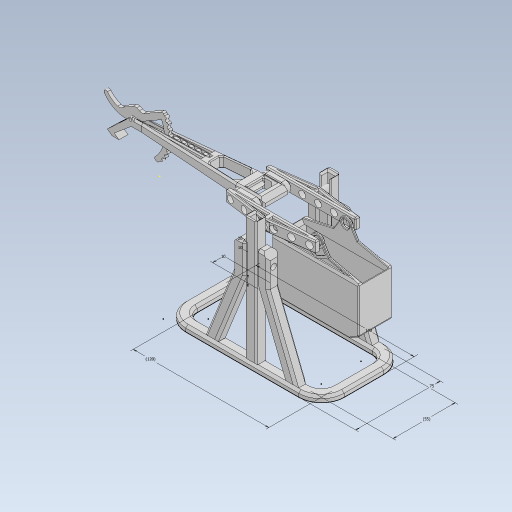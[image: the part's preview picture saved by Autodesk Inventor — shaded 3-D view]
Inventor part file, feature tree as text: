
AUTODESK INVENTOR PART (.ipt)
format: ipt  version: 2023 (Build 270158030, 158C)  size: 2,069,504 bytes
history: native  units: mm
features: extrude x39, sketch x36, chamfer x34, other x22, projected_geometry x16, mirror x11, fillet x10, plane x5, pattern_circular x2
ambient origin geometry x8: Origin, YZ Plane, XZ Plane, XY Plane, X Axis, Y Axis, Z Axis, Center Point
bodies: SOLID_WEIGHT (feature_tree)
feature tree (175):
  other  "baseplate"
  sketch  "Sketch1"  dims[d0=75.0mm d1=140.0mm]
  extrude  "Extrusion1"  Depth=140.0mm
  extrude  "Extrusion2"  Depth=10.0mm
  sketch  "Sketch3"  dims[d4=20.0mm d5=5.0mm d6=0.0mm]
  extrude  "Extrusion5"  Depth=5.0mm TaperAngle=0.0deg
  extrude  "Extrusion6"  Depth=2.0mm
  extrude  "Extrusion3"  Depth=3.0mm
  extrude  "Extrusion7"  Depth=10.0mm
  extrude  "Extrusion9"  TaperAngle=0.0deg  [1 undecoded]
  extrude  "Extrusion10"  Depth=120.0mm
  extrude  "Extrusion11"  Depth=0.01mm
  extrude  "Extrusion29"  Depth=10.0mm
  other  "center-mirror-plane"
  other  "Work Point1"
  plane  "Work Plane2"
  extrude  "Extrusion12"  Depth=25.0mm
  extrude  "Extrusion13"  Depth=5.0mm TaperAngle=0.0deg
  extrude  "Extrusion14"  Depth=10.0mm
  extrude  "Extrusion15"  Depth=10.0mm TaperAngle=0.0deg
  extrude  "Extrusion30"  Depth=5.0mm
  extrude  "Extrusion31"  Depth=6.5mm
  plane  "Work Plane5"
  extrude  "Extrusion32"  Depth=1.75mm
  extrude  "Extrusion33"  Depth=6.5mm
  extrude  "Extrusion34"  Depth=10.0mm
  fillet  "Fillet4"  Radius=3.2mm
  chamfer  "Chamfer37"  Distance=10.0mm
  extrude  "Extrusion35"  Depth=4.0mm
  chamfer  "Chamfer38"  [1 undecoded]
  fillet  "Fillet11"  Radius=21.0mm
  chamfer  "Chamfer39"  [1 undecoded]
  fillet  "Fillet12"  Radius=6.0mm
  extrude  "Extrusion36"  Depth=2.0mm
  fillet  "Fillet5"  Radius=10.0mm
  extrude  "Extrusion37"  Depth=2.0mm TaperAngle=45.0deg
  sketch  "Sketch51"  dims[d109=12.0mm d110=0.0mm d111=0.0mm d119=6.0mm d120=5.0mm d121=10.0mm d122=0.0mm d126=1.0mm d127=2.0mm d128=45.0deg d129=1.0mm d130=2.0mm d131=45.0deg d132=1.0mm d133=2.0mm d134=45.0deg d135=1.5mm d136=2.0mm d137=45.0deg d138=2.5mm d139=2.8mm d140=12.0mm d141=0.0mm d142=0.0mm d144=6.0mm d145=2.0mm d146=2.0mm d147=45.0deg d155=1.0mm d156=2.0mm d157=45.0deg d158=1.5mm d159=2.0mm d160=45.0deg d162=1.5mm d163=2.0mm d164=45.0deg d165=2.0mm d166=2.0mm d167=45.0deg d168=1.5mm d169=2.0mm d170=45.0deg d172=2.0mm d173=8.0mm d174=5.0mm d175=28.0mm d176=6.0mm d177=40.0mm d178=5.0mm d179=28.0mm d180=8.0mm d181=8.0mm d182=2.0mm d183=2.0mm d184=0.0mm d185=2.0mm d186=0.0mm d187=1.5mm d188=0.0mm d189=1.5mm d190=2.0mm d191=45.0deg d195=1.0mm d196=1.5mm d197=0.0mm d200=1.0mm d201=2.0mm d202=45.0deg d209=0.5mm d210=2.0mm d211=45.0deg d212=0.5mm d213=2.0mm d214=45.0deg d221=0.0mm d222=0.0mm d223=1.0mm d224=1.0mm d227=0.0mm d228=0.0mm d232=4.0mm d233=2.0mm d234=45.0deg d235=1.0mm d236=2.0mm d237=45.0deg d238=1.2mm d239=2.0mm d240=45.0deg d241=1.2mm d242=3.0mm d247=2.0mm d248=2.0mm d249=2.0mm d250=0.9mm d252=20.0mm d254=15.996982mm d255=8.0mm d256=6.0mm d257=6.0mm d258=6.0mm d259=5.0mm d260=5.0mm d261=14.0mm d262=14.0mm d263=0.0mm d264=0.0mm d271=3.5mm d272=2.0mm d273=45.0deg d274=3.5mm d275=2.0mm d276=45.0deg d287=1.5mm d288=2.0mm d289=45.0deg d290=1.9mm d291=10.0mm d292=0.0mm d298=3.0mm d299=0.5mm d300=0.0mm d303=3.5mm d304=3.0mm d305=0.5mm d306=0.0mm d307=2.0mm d308=1.5mm d309=0.5mm d310=0.0mm d311=0.0mm d312=5.0mm d313=10.0mm d314=0.8mm d315=27.1mm d316=3.2mm d317=0.0mm d319=0.0mm d320=0.0mm d321=36.0mm d322=0.4mm d323=0.4mm d324=3.5mm d328=3.2mm d329=0.0mm d330=2.0mm d331=4.0mm d336=6.0mm d337=3.2mm d338=0.0mm d342=3.2mm d343=3.2mm d344=3.2mm d345=3.2mm d346=3.2mm d347=3.2mm d348=3.2mm d349=3.2mm d350=3.2mm d351=1.9mm d352=0.0mm d353=4.0mm d363=19.6mm d364=19.5mm d366=3.0mm d367=90.0deg d368=23.0mm d377=10.0mm d386=2.9mm d387=0.0mm d394=1.7mm d395=1.5mm d396=4.4mm d398=3.5mm d399=2.0mm d400=45.0deg d401=3.0mm d402=2.0mm d403=45.0deg d404=4.0mm d405=1.8mm d406=2.0mm d407=45.0deg d408=4.0mm d415=4.0mm d426=1.5mm d431=7.0mm d432=0.0mm d433=0.0mm d434=4.0mm d435=2.0mm d436=2.0mm d437=45.0deg d438=1.0mm d439=2.4mm d440=0.0mm d441=0.8mm d442=2.5mm d443=2.5mm d444=1.5mm d445=1.5mm d446=3.0mm d447=14.0mm d448=14.0mm d449=14.0mm d450=10.0mm d451=0.0mm d452=1.5mm d453=1.5mm d454=4.0mm d455=0.0mm d456=2.0mm d457=2.0mm d458=45.0deg d459=3.0mm d460=2.0mm d461=45.0deg d462=1.0mm d463=2.0mm d464=45.0deg d465=12.0mm d466=12.0mm d467=5.0mm d468=25.0mm d469=5.0mm d470=3.0mm d471=0.8mm d472=2.0mm d473=45.0deg d474=1.5mm d475=0.15mm d476=5.0mm d477=0.0mm d478=0.6mm d479=2.0mm d480=45.0deg d481=5.0mm d483=38.5mm d484=38.5mm d485=2.5mm d491=2.0mm d492=30.0deg d493=14.0mm d494=0.5mm d495=2.0mm d496=45.0deg d497=2.5mm d498=2.5mm d499=30.0deg d500=1.5mm d501=0.0mm d505=11.0mm d506=5.0mm d507=2.0mm d508=45.0deg d509=6.981317mm d510=75.0deg d511=20.0mm d512=0.4mm d514=10.293981mm d520=1.5mm d521=63.0mm d522=3.2mm d523=30.0deg d524=4.0mm d525=75.0deg d526=35.0mm d527=5.072433mm d528=2.3mm d529=4.5mm d530=1.2mm d531=2.9mm d532=0.0mm d533=1.5mm d534=0.0mm d535=0.0mm d542=40.0mm d543=4.363323mm d545=50.0mm d546=5.759587mm d548=5.5mm d549=38.0mm d550=10.902886mm d551=5.0mm d552=2.0mm d553=45.0deg d554=1.0mm d555=2.0mm d556=45.0deg d557=2.0mm d558=2.0mm d559=0.0mm d560=1.0mm d561=2.0mm d562=45.0deg]
  extrude  "Extrusion45"  Depth=2.0mm TaperAngle=45.0deg
  extrude  "Extrusion46"  Depth=2.0mm TaperAngle=45.0deg
  pattern_circular  "Circular Pattern3"  Angle=45.0deg  [1 undecoded]
  pattern_circular  "Circular Pattern4"  [2 undecoded]
  fillet  "Fillet13"  Radius=2.8mm
  fillet  "Fillet15"  Radius=12.0mm
  fillet  "Fillet10"  [1 undecoded]
  extrude  "Extrusion17"  Depth=2.0mm
  extrude  "Extrusion26"  Depth=2.0mm TaperAngle=45.0deg
  extrude  "Extrusion38"  Depth=2.0mm TaperAngle=45.0deg
  fillet  "Fillet16"  Radius=2.0mm
  chamfer  "Chamfer1"  Distance=2.0mm Angle=45.0deg
  chamfer  "Chamfer2"  Distance=2.0mm Angle=45.0deg
  chamfer  "Chamfer3"  Distance=2.0mm Angle=45.0deg
  chamfer  "Chamfer4"  Distance=2.0mm
  extrude  "Extrusion19"  Depth=2.0mm
  chamfer  "Chamfer5"  Distance=5.0mm
  chamfer  "Chamfer8"  Distance=28.0mm
  chamfer  "Chamfer9"  Distance=6.0mm
  chamfer  "Chamfer10"  Distance=40.0mm
  chamfer  "Chamfer43"  Distance=5.0mm
  extrude  "Extrusion39"  Depth=2.0mm
  mirror  "Mirror12"
  chamfer  "Chamfer11"  Distance=8.0mm
  chamfer  "Chamfer50"  Distance=8.0mm
  chamfer  "Chamfer12"  Distance=2.0mm
  plane  "Work Plane4"
  extrude  "CW-extrusion"  Depth=2.0mm TaperAngle=0.0deg
  mirror  "Mirror3"
  extrude  "Extrusion21"  Depth=2.0mm TaperAngle=0.0deg
  extrude  "Extrusion22"  Depth=2.0mm TaperAngle=0.0deg
  mirror  "Mirror4"
  chamfer  "Chamfer13"  Distance=2.0mm Angle=45.0deg
  extrude  "Extrusion23"  Depth=2.0mm TaperAngle=0.0deg
  mirror  "Mirror5"
  chamfer  "Chamfer31"  Distance=2.0mm Angle=45.0deg
  chamfer  "Chamfer14"  Distance=2.0mm Angle=45.0deg
  chamfer  "Chamfer17"  Distance=2.0mm Angle=45.0deg
  chamfer  "Chamfer18"  [1 undecoded]
  extrude  "Extrusion24"  Depth=2.0mm
  extrude  "Extrusion25"  Depth=2.0mm
  chamfer  "Chamfer20"  [1 undecoded]
  chamfer  "Chamfer49"  Distance=4.0mm Angle=45.0deg
  chamfer  "Chamfer21"  Distance=2.0mm Angle=45.0deg
  extrude  "Extrusion40"  Depth=1.2mm TaperAngle=45.0deg
  extrude  "Extrusion41"  Depth=1.2mm
  chamfer  "Chamfer22"  Distance=3.0mm
  chamfer  "Chamfer44"  Distance=2.0mm
  chamfer  "Chamfer45"  Distance=2.0mm
  chamfer  "Chamfer46"  Distance=2.0mm
  fillet  "Fillet3"  Radius=0.9mm
  mirror  "Mirror2"
  mirror  "Mirror1"
  plane  "Work Plane3"
  mirror  "Mirror6"
  mirror  "Mirror7"
  mirror  "Mirror8"
  chamfer  "Chamfer26"  Distance=20.0mm
  chamfer  "Chamfer27"  Distance=15.996982mm
  extrude  "Extrusion43"  Depth=2.0mm
  mirror  "Mirror10"
  chamfer  "Chamfer47"  Distance=6.0mm
  extrude  "Extrusion42"  Depth=2.0mm
  chamfer  "Chamfer48"  Distance=6.0mm
  mirror  "Mirror11"
  sketch  "Sketch35"  dims[d79=40.0mm]
  plane  "Work Plane6"
  chamfer  "Chamfer51"  Distance=5.0mm
  chamfer  "Chamfer52"  Distance=5.0mm
  fillet  "Fillet17"  Radius=14.0mm
  chamfer  "Chamfer53"  Distance=14.0mm
  sketch  "Sketch2"  dims[d2=10.0mm d3=10.0mm]
  sketch  "Sketch4"  dims[d7=6.0mm d9=2.0mm]
  projected_geometry  "Projected Loop1"
  other  "A-frame"
  sketch  "Sketch7"  dims[d10=10.0mm d11=3.0mm]
  projected_geometry  "Projected Loop2"
  other  "upright"
  projected_geometry  "Projected Loop3"
  sketch  "Sketch10"  dims[d12=1.75mm d13=6.0mm d14=10.0mm]
  sketch  "Sketch12"  dims[d15=60.0mm d16=0.0mm d17=0.0mm]
  sketch  "Sketch13"  dims[d18=55.0mm d19=120.0mm]
  sketch  "Sketch14"  dims[d22=0.1mm d23=0.01mm]
  other  "pivot"
  sketch  "Sketch16"  dims[d24=5.0mm d25=0.0mm d38=10.0mm]
  other  "throw-arm-top"
  sketch  "Sketch18"  dims[d39=25.0mm d40=25.0mm]
  sketch  "Sketch20"  dims[d41=0.01mm d42=5.0mm d43=5.0mm d44=0.0mm d45=0.0mm]
  sketch  "Sketch22"  dims[d47=10.0mm d50=10.0mm]
  other  "counterweight"
  projected_geometry  "Projected Loop5"
  sketch  "Sketch26"  dims[d51=110.0mm d52=0.0mm d53=10.0mm d54=0.0mm]
  projected_geometry  "Projected Loop6"
  sketch  "Sketch27"  dims[d60=5.0mm d61=5.0mm]
  projected_geometry  "Projected Loop7"
  sketch  "Sketch29"  dims[d64=0.0mm d65=0.0mm d66=6.5mm]
  sketch  "Sketch30"  dims[d67=1.75mm d68=1.75mm]
  other  "Pattern of pivot:1"
  other  "pivot-mirror"
  other  "Pattern of upright:2"
  other  "upright-mirror"
  other  "Pattern of A-frame:3"
  other  "A-frame-b"
  other  "Pattern of A-frame:4"
  other  "A-frame-c"
  other  "Pattern of A-frame-b:5"
  other  "A-frame-d"
  sketch  "Sketch31"  dims[d69=11.0mm d70=6.5mm]
  projected_geometry  "Projected Loop8"
  sketch  "Sketch32"  dims[d71=7.0mm d72=0.0mm d73=6.0mm d74=3.2mm d75=10.0mm d76=0.0mm]
  projected_geometry  "Projected Loop9"
  sketch  "Sketch34"  dims[d77=4.0mm d78=40.0mm]
  sketch  "Sketch36"  dims[d80=5.0mm]
  sketch  "Sketch37"  dims[d83=4.0mm]
  sketch  "Sketch38"  dims[d84=29.0mm]
  projected_geometry  "Projected Loop15"
  projected_geometry  "Projected Loop16"
  sketch  "Sketch39"  dims[d85=2.0mm d86=8.0mm d87=0.0mm d88=0.0mm]
  sketch  "Sketch40"  dims[d89=6.0mm]
  projected_geometry  "Projected Loop17"
  sketch  "Sketch41"  dims[d90=5.0mm]
  sketch  "Sketch42"  dims[d91=5.0mm d92=0.0mm d93=0.0mm d96=21.0mm]
  sketch  "Sketch43"  dims[d99=8.0mm]
  other  "ratchet"
  sketch  "Sketch44"  dims[d100=10.0mm]
  sketch  "Sketch45"  dims[d101=6.5mm]
  projected_geometry  "Projected Loop18"
  projected_geometry  "Projected Loop19"
  sketch  "Sketch46"  dims[d102=6.5mm]
  sketch  "Sketch47"  dims[d103=125.0mm]
  projected_geometry  "Projected Loop20"
  sketch  "Sketch48"  dims[d104=10.0mm d105=5.0mm d106=0.0mm d107=0.0mm]
  other  "spacer-a"
  other  "Pattern of spacer-a:6"
  other  "spacer-b"
  projected_geometry  "Projected Loop24"
  sketch  "Sketch49"  dims[d108=7.0mm]
  projected_geometry  "Projected Loop25"
note: 9 required parameter values undecoded (feature->parameter linkage not recoverable at this tier; creation-order binding heuristic only, values carry confidence <= 0.55)
